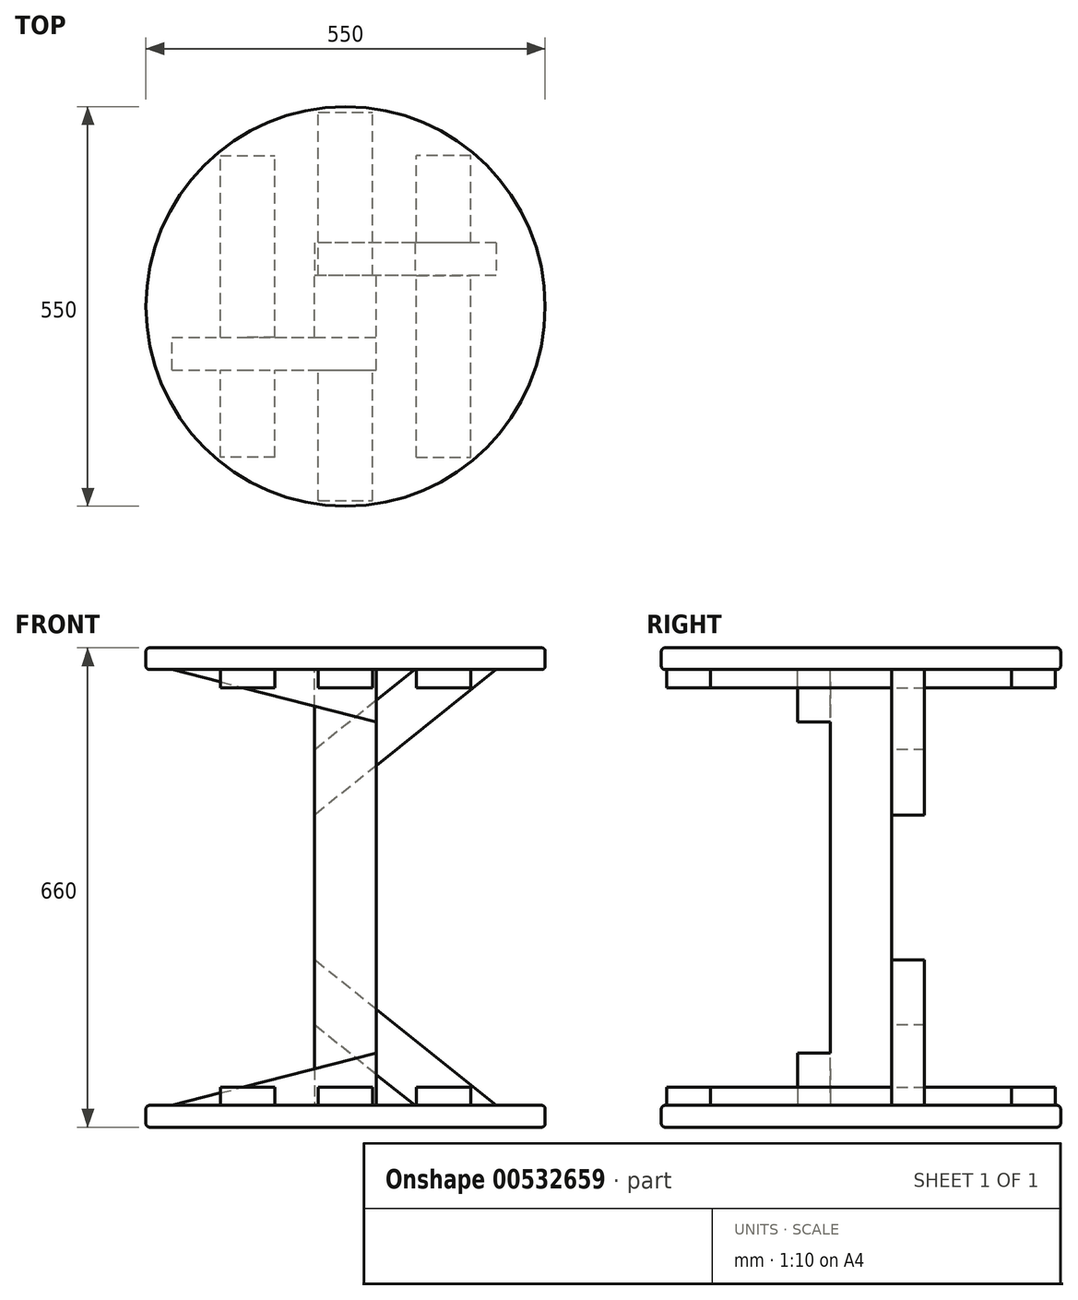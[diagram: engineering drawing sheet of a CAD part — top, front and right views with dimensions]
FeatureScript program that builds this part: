
annotation { "Feature Type Name" : "Feature", "Feature Type Description" : "" }
export const myFeature = defineFeature(function(context is Context, id is Id, definition is map)
    precondition{}
    {
        {
            var Q0;
            Q0=qCreatedBy(makeId("Top.planeOp"),FACE);
            var sketch = newSketch(context, id + "F0", { "sketchPlane" : qUnion([Q0])});
            skCircle(sketch, "E0", {"center": v(0, 0) * mm, "radius": 275 * mm});
            skSolve(sketch);
        }
        {
            var Q0;
            Q0 = qSketchRegion(id + "F0", true);
            extrude(context, id + "F1", {"entities" : qUnion([Q0]), "depth" : 30 * mm, "offsetDistance" : 25 * mm});
        }
        {
            var Q0;
            Q0=makeQuery(id+"F1.opExtrude","CAP_FACE",FACE,{"disambiguationData":[OSD([sQuery(id+"F0.wireOp",EDGE,"E0")])],"isStart":true});
            var sketch = newSketch(context, id + "F2", { "sketchPlane" : qUnion([Q0])});
            skLineSegment(sketch, "E1.bottom", {"start": v(42.5, 42.5) * mm, "end": v(-42.5, 42.5) * mm});
            skLineSegment(sketch, "E1.top", {"start": v(42.5, -42.5) * mm, "end": v(-42.5, -42.5) * mm});
            skLineSegment(sketch, "E1.left", {"start": v(42.5, 42.5) * mm, "end": v(42.5, -42.5) * mm});
            skLineSegment(sketch, "E1.right", {"start": v(-42.5, 42.5) * mm, "end": v(-42.5, -42.5) * mm});
            skPoint(sketch, "E1.middle", {"position": v(0, 0) * mm});
            skSolve(sketch);
        }
        {
            var Q0;
            Q0 = qSketchRegion(id + "F2", true);
            extrude(context, id + "F3", {"entities" : qUnion([Q0]), "operationType" : NewBodyOperationType.ADD, "depth" : 300 * mm, "offsetDistance" : 25 * mm});
        }
        {
            var Q0;
            Q0=makeQuery(id+"F1.opExtrude","CAP_FACE",FACE,{"disambiguationData":[OSD([sQuery(id+"F0.wireOp",EDGE,"E0")])],"isStart":true});
            var sketch = newSketch(context, id + "F4", { "sketchPlane" : qUnion([Q0])});
            skLineSegment(sketch, "E2.MirrorCS", {"start": v(37.5, -42.5) * mm, "end": v(37.5, -267.5) * mm});
            skLineSegment(sketch, "E3.MirrorCS", {"start": v(-37.5, -267.5) * mm, "end": v(0, -267.5) * mm});
            skLineSegment(sketch, "E4.MirrorCS", {"start": v(0, -267.5) * mm, "end": v(37.5, -267.5) * mm});
            skLineSegment(sketch, "E5.MirrorCS", {"start": v(-37.5, -42.5) * mm, "end": v(-37.5, -267.5) * mm});
            skLineSegment(sketch, "E6.MirrorCS", {"start": v(-37.5, -42.5) * mm, "end": v(0, -42.5) * mm});
            skLineSegment(sketch, "E7.MirrorCS", {"start": v(0, -42.5) * mm, "end": v(37.5, -42.5) * mm});
            skLineSegment(sketch, "E8", {"start": v(-97.5, 207.5) * mm, "end": v(-97.5, 87.5) * mm});
            skLineSegment(sketch, "E9", {"start": v(-97.5, 207.5) * mm, "end": v(-172.5, 207.5) * mm});
            skLineSegment(sketch, "E10", {"start": v(-172.5, 207.5) * mm, "end": v(-172.5, 87.5) * mm});
            skLineSegment(sketch, "E11", {"start": v(-172.5, -207.5) * mm, "end": v(-97.5, -207.5) * mm});
            skLineSegment(sketch, "E12.MirrorCS", {"start": v(97.5, 207.5) * mm, "end": v(172.5, 207.5) * mm});
            skLineSegment(sketch, "E13.MirrorCS", {"start": v(172.5, 207.5) * mm, "end": v(172.5, -42.5) * mm});
            skLineSegment(sketch, "E14.MirrorCS", {"start": v(172.5, -207.5) * mm, "end": v(97.5, -207.5) * mm});
            skLineSegment(sketch, "E15", {"start": v(-97.5, 42.5) * mm, "end": v(-172.5, 42.5) * mm});
            skLineSegment(sketch, "E16", {"start": v(-172.5, 87.5) * mm, "end": v(-97.5, 87.5) * mm});
            skLineSegment(sketch, "E17.trimOffspring", {"start": v(-172.5, 42.5) * mm, "end": v(-172.5, -207.5) * mm});
            skLineSegment(sketch, "E18.trimOffspring", {"start": v(-97.5, 42.5) * mm, "end": v(-97.5, -207.5) * mm});
            skLineSegment(sketch, "E19", {"start": v(97.5, -42.5) * mm, "end": v(172.5, -42.5) * mm});
            skLineSegment(sketch, "E20", {"start": v(172.5, -87.5) * mm, "end": v(97.5, -87.5) * mm});
            skLineSegment(sketch, "E21.trimOffspring", {"start": v(172.5, -87.5) * mm, "end": v(172.5, -207.5) * mm});
            skLineSegment(sketch, "E22.trimOffspring", {"start": v(97.5, -87.5) * mm, "end": v(97.5, -207.5) * mm});
            skPoint(sketch, "E23.MirrorCS.start.orphan", {"position": v(97.5, 207.5) * mm});
            skLineSegment(sketch, "E24", {"start": v(97.5, 207.5) * mm, "end": v(97.5, -42.5) * mm});
            skLineSegment(sketch, "E25", {"start": v(-37.5, 267.5) * mm, "end": v(-37.5, 87.5) * mm});
            skLineSegment(sketch, "E26", {"start": v(37.5, 267.5) * mm, "end": v(37.5, 87.5) * mm});
            skLineSegment(sketch, "E27", {"start": v(-37.5, 267.5) * mm, "end": v(37.5, 267.5) * mm});
            skLineSegment(sketch, "E28", {"start": v(-37.5, 87.5) * mm, "end": v(37.5, 87.5) * mm});
            skSolve(sketch);
        }
        {
            var Q0;
            Q0 = qSketchRegion(id + "F4", true);
            extrude(context, id + "F5", {"entities" : qUnion([Q0]), "operationType" : NewBodyOperationType.ADD, "depth" : 25 * mm, "offsetDistance" : 25 * mm});
        }
        {
            var Q0;
            Q0=makeQuery(id+"F3.opExtrude","SWEPT_FACE",FACE,{"disambiguationData":[OSD([sQuery(id+"F2.wireOp",EDGE,"E1.bottom")])]});
            var sketch = newSketch(context, id + "F6", { "sketchPlane" : qUnion([Q0])});
            skLineSegment(sketch, "E29", {"start": v(42.5, 0) * mm, "end": v(42.5, 0) * mm});
            skLineSegment(sketch, "E30", {"start": v(-239.06, 0) * mm, "end": v(42.5, -72.27) * mm});
            skLineSegment(sketch, "E31", {"start": v(-239.06, 0) * mm, "end": v(42.5, 0) * mm});
            skLineSegment(sketch, "E32", {"start": v(42.5, -72.27) * mm, "end": v(42.5, 0) * mm});
            skSolve(sketch);
        }
        {
            var Q0;
            Q0 = qSketchRegion(id + "F6", true);
            extrude(context, id + "F7", {"entities" : qUnion([Q0]), "operationType" : NewBodyOperationType.ADD, "depth" : 45 * mm, "offsetDistance" : 25 * mm});
        }
        {
            var Q0;
            Q0=makeQuery(id+"F3.opExtrude","SWEPT_FACE",FACE,{"disambiguationData":[OSD([sQuery(id+"F2.wireOp",EDGE,"E1.top")])]});
            var sketch = newSketch(context, id + "F8", { "sketchPlane" : qUnion([Q0])});
            skLineSegment(sketch, "E33", {"start": v(-95.5, 0) * mm, "end": v(42.5, -110.49) * mm});
            skLineSegment(sketch, "E34", {"start": v(-207.5, 0) * mm, "end": v(42.5, -200.16) * mm});
            skLineSegment(sketch, "E35", {"start": v(-207.5, 0) * mm, "end": v(-95.5, 0) * mm});
            skLineSegment(sketch, "E36", {"start": v(42.5, -110.49) * mm, "end": v(42.5, -200.16) * mm});
            skSolve(sketch);
        }
        {
            var Q0;
            Q0 = qSketchRegion(id + "F8", true);
            extrude(context, id + "F9", {"entities" : qUnion([Q0]), "operationType" : NewBodyOperationType.ADD, "depth" : 45 * mm, "offsetDistance" : 25 * mm});
        }
        {
            var Q0;
            Q0=makeQuery(id+"F3.opExtrude","CAP_FACE",FACE,{"disambiguationData":[OSD([sQuery(id+"F2.wireOp",EDGE,"E1.bottom"),sQuery(id+"F2.wireOp",EDGE,"E1.top"),sQuery(id+"F2.wireOp",EDGE,"E1.left"),sQuery(id+"F2.wireOp",EDGE,"E1.right")])],"isStart":false});
            cPlane(context, id + "F10", {"entities" : qUnion([Q0]), "cplaneType" : CPlaneType.OFFSET, "offset" : 0 * mm, "width" : 150 * mm, "height" : 150 * mm});
        }
        {
            var Q0;
            Q0=makeQuery(id+"F1.opExtrude","CAP_EDGE",EDGE,{"disambiguationData":[OSD([sQuery(id+"F0.wireOp",EDGE,"E0")])],"isStart":false});
            var Q1;
            Q1=makeQuery(id+"F5.boolean.opBoolean","SPLIT",EDGE,{"disambiguationData":[OD(0.0)],"derivedFrom":makeQuery(id+"F1.opExtrude","CAP_EDGE",EDGE,{"disambiguationData":[OSD([sQuery(id+"F0.wireOp",EDGE,"E0")])],"isStart":true})});
            fillet(context, id + "F11", {"entities" : qUnion([Q0, Q1]), "radius" : 5 * mm, "tangentPropagation" : true, "allowEdgeOverflow" : false});
        }
        {
            var Q0;
            Q0=makeQuery(id+"F1.opExtrude","SWEPT_BODY",BODY,{"disambiguationData":[OSD([sQuery(id+"F0.wireOp",EDGE,"E0")])]});
            var Q1;
            Q1=qCreatedBy(id+"F10.planeOp",FACE);
            mirror(context, id + "F12", {"operationType" : NewBodyOperationType.ADD, "entities" : qUnion([Q0]), "mirrorPlane" : qUnion([Q1])});
        }
    });
